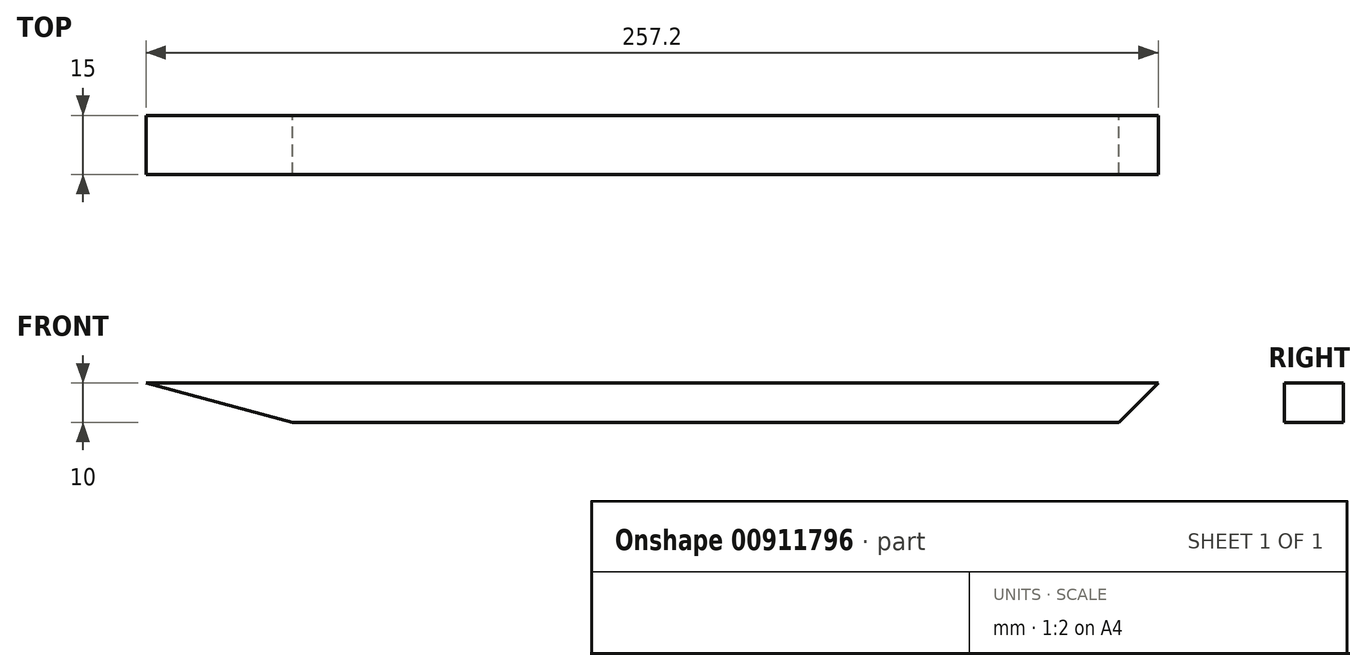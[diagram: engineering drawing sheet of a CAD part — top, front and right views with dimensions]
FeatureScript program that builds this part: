
annotation { "Feature Type Name" : "Feature", "Feature Type Description" : "" }
export const myFeature = defineFeature(function(context is Context, id is Id, definition is map)
    precondition{}
    {
        {
            var Q0;
            Q0=qCreatedBy(makeId("Front.planeOp"),FACE);
            var sketch = newSketch(context, id + "F0", { "sketchPlane" : qUnion([Q0])});
            skLineSegment(sketch, "E0", {"start": v(-104.94, 0) * mm, "end": v(104.94, 0) * mm});
            skPoint(sketch, "E1", {"position": v(0, -2.6) * mm});
            skLineSegment(sketch, "E2", {"start": v(-142.26, 10) * mm, "end": v(-104.94, 0) * mm});
            skLineSegment(sketch, "E3", {"start": v(114.94, 10) * mm, "end": v(104.94, 0) * mm});
            skLineSegment(sketch, "E4", {"start": v(-142.26, 10) * mm, "end": v(114.94, 10) * mm});
            skSolve(sketch);
        }
        {
            var Q0;
            Q0=makeQuery(id+"F0.imprint","IMPRINT",FACE,{"disambiguationData":[TD([[makeQuery(id+"F0.imprint","IMPRINT",EDGE,{"derivedFrom":sQuery(id+"F0.wireOp",EDGE,"E0")}),1.0]])]});
            extrude(context, id + "F1", {"entities" : qUnion([Q0]), "depth" : 15 * mm, "offsetDistance" : 25 * mm});
        }
    });
